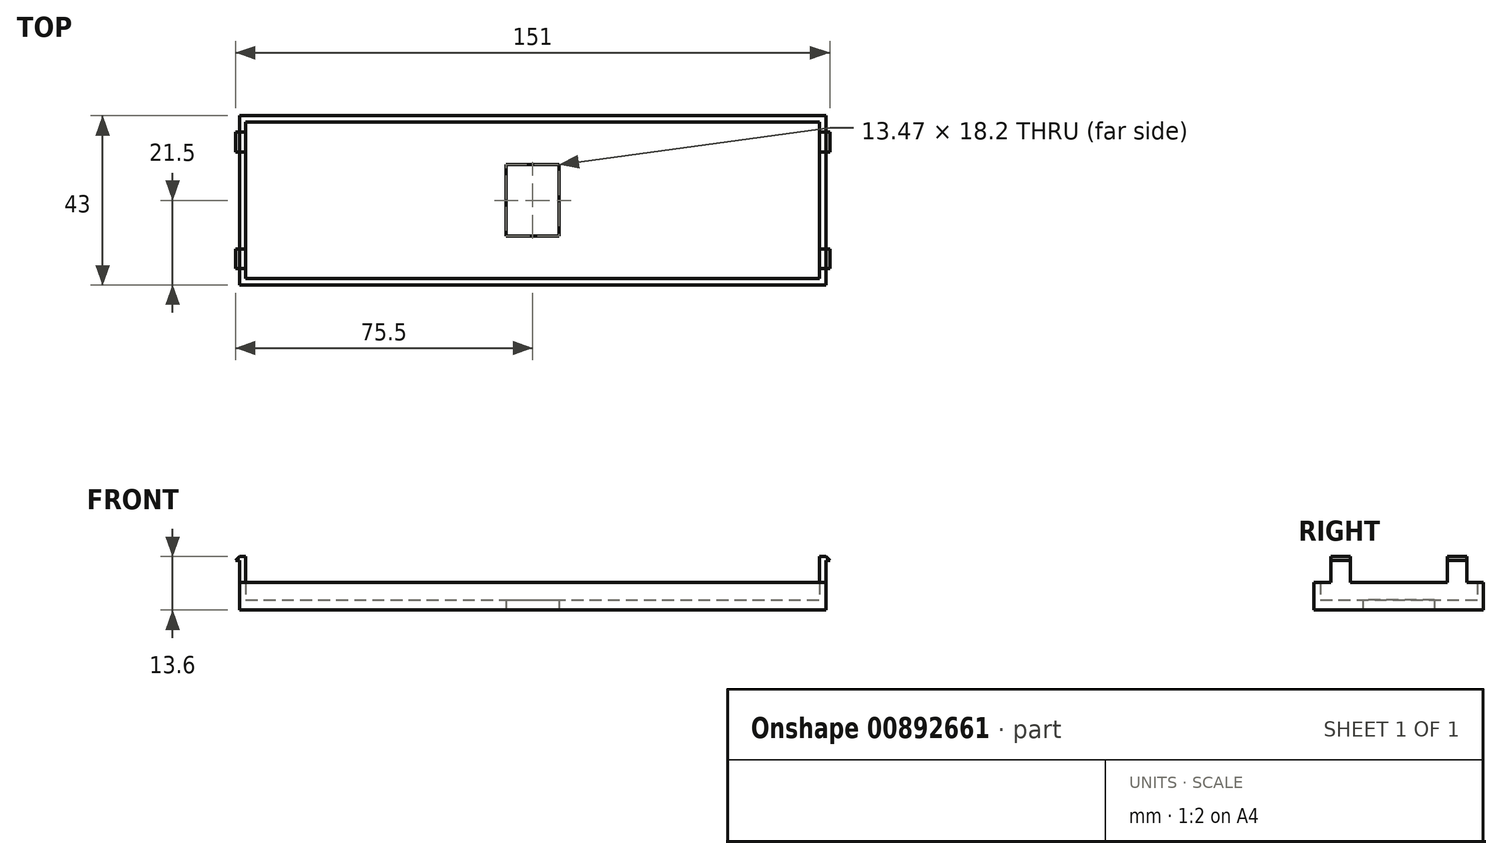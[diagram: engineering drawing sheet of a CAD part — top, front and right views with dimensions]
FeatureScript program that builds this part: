
annotation { "Feature Type Name" : "Feature", "Feature Type Description" : "" }
export const myFeature = defineFeature(function(context is Context, id is Id, definition is map)
    precondition{}
    {
        {
            var Q0;
            Q0=qCreatedBy(makeId("Top.planeOp"),FACE);
            var sketch = newSketch(context, id + "F0", { "sketchPlane" : qUnion([Q0])});
            skLineSegment(sketch, "E0", {"start": v(0, 0) * mm, "end": v(149, 0) * mm});
            skLineSegment(sketch, "E1", {"start": v(149, 0) * mm, "end": v(149, -43) * mm});
            skLineSegment(sketch, "E2", {"start": v(149, -43) * mm, "end": v(0, -43) * mm});
            skLineSegment(sketch, "E3", {"start": v(0, -43) * mm, "end": v(0, 0) * mm});
            skSolve(sketch);
        }
        {
            var Q0;
            Q0 = qSketchRegion(id + "F0", true);
            extrude(context, id + "F1", {"entities" : qUnion([Q0]), "depth" : 7 * mm, "offsetDistance" : 25 * mm});
        }
        {
            var Q0;
            Q0=makeQuery(id+"F1.opExtrude","CAP_FACE",FACE,{"disambiguationData":[OSD([sQuery(id+"F0.wireOp",EDGE,"E0"),sQuery(id+"F0.wireOp",EDGE,"E1"),sQuery(id+"F0.wireOp",EDGE,"E2"),sQuery(id+"F0.wireOp",EDGE,"E3")])],"isStart":false});
            shell(context, id + "F2", {"entities" : qUnion([Q0]), "thickness" : 1.6 * mm});
        }
        {
            var Q0;
            Q0=makeQuery(id+"F2.opShell","OFFSET_FACE",FACE,{"disambiguationData":[OSD([sQuery(id+"F0.wireOp",EDGE,"E0"),sQuery(id+"F0.wireOp",EDGE,"E1"),sQuery(id+"F0.wireOp",EDGE,"E2"),sQuery(id+"F0.wireOp",EDGE,"E3")])]});
            extrude(context, id + "F3", {"entities" : qUnion([Q0]), "operationType" : NewBodyOperationType.ADD, "depth" : 1 * mm, "offsetDistance" : 25 * mm});
        }
        {
            var Q0;
            Q0=makeQuery(id+"F1.opExtrude","CAP_FACE",FACE,{"disambiguationData":[OSD([sQuery(id+"F0.wireOp",EDGE,"E0"),sQuery(id+"F0.wireOp",EDGE,"E1"),sQuery(id+"F0.wireOp",EDGE,"E2"),sQuery(id+"F0.wireOp",EDGE,"E3")])],"isStart":false});
            var sketch = newSketch(context, id + "F4", { "sketchPlane" : qUnion([Q0])});
            skLineSegment(sketch, "E4", {"start": v(1.6, -4.2) * mm, "end": v(0, -4.2) * mm});
            skLineSegment(sketch, "E5", {"start": v(0, -4.2) * mm, "end": v(0, -9.2) * mm});
            skLineSegment(sketch, "E6", {"start": v(0, -9.2) * mm, "end": v(1.6, -9.2) * mm});
            skLineSegment(sketch, "E7", {"start": v(1.6, -9.2) * mm, "end": v(1.6, -4.2) * mm});
            skLineSegment(sketch, "E8", {"start": v(74.5, -1.6) * mm, "end": v(74.5, -47.8) * mm});
            skLineSegment(sketch, "E9.bottom", {"start": v(0, -38.8) * mm, "end": v(1.6, -38.8) * mm});
            skLineSegment(sketch, "E9.top", {"start": v(0, -33.8) * mm, "end": v(1.6, -33.8) * mm});
            skLineSegment(sketch, "E9.left", {"start": v(0, -38.8) * mm, "end": v(0, -33.8) * mm});
            skLineSegment(sketch, "E9.right", {"start": v(1.6, -38.8) * mm, "end": v(1.6, -33.8) * mm});
            skLineSegment(sketch, "E10.MirrorCS", {"start": v(147.4, -9.2) * mm, "end": v(147.4, -4.2) * mm});
            skLineSegment(sketch, "E11.MirrorCS", {"start": v(147.4, -4.2) * mm, "end": v(149, -4.2) * mm});
            skLineSegment(sketch, "E12.MirrorCS", {"start": v(149, -4.2) * mm, "end": v(149, -9.2) * mm});
            skLineSegment(sketch, "E13.MirrorCS", {"start": v(149, -9.2) * mm, "end": v(147.4, -9.2) * mm});
            skLineSegment(sketch, "E14.MirrorCS", {"start": v(149, -33.8) * mm, "end": v(147.4, -33.8) * mm});
            skLineSegment(sketch, "E15.MirrorCS", {"start": v(149, -38.8) * mm, "end": v(149, -33.8) * mm});
            skLineSegment(sketch, "E16.MirrorCS", {"start": v(147.4, -38.8) * mm, "end": v(147.4, -33.8) * mm});
            skLineSegment(sketch, "E17.MirrorCS", {"start": v(149, -38.8) * mm, "end": v(147.4, -38.8) * mm});
            skSolve(sketch);
        }
        {
            var Q0;
            Q0 = qSketchRegion(id + "F4", true);
            extrude(context, id + "F5", {"entities" : qUnion([Q0]), "operationType" : NewBodyOperationType.ADD, "depth" : 6.6 * mm, "offsetDistance" : 25 * mm});
        }
        {
            var Q0;
            Q0=makeQuery(id+"F5.boolean.opBoolean","MERGE",FACE,{"derivedFrom":[makeQuery(id+"F1.opExtrude","SWEPT_FACE",FACE,{"disambiguationData":[OSD([sQuery(id+"F0.wireOp",EDGE,"E3")])]}),makeQuery(id+"F5.opExtrude","SWEPT_FACE",FACE,{"disambiguationData":[OSD([sQuery(id+"F4.wireOp",EDGE,"E5")])]}),makeQuery(id+"F5.opExtrude","SWEPT_FACE",FACE,{"disambiguationData":[OSD([sQuery(id+"F4.wireOp",EDGE,"E9.left")])]})]});
            var sketch = newSketch(context, id + "F6", { "sketchPlane" : qUnion([Q0])});
            skLineSegment(sketch, "E18.bottom", {"start": v(4.2, 13.6) * mm, "end": v(9.2, 13.6) * mm});
            skLineSegment(sketch, "E18.top", {"start": v(4.2, 12.56) * mm, "end": v(9.2, 12.56) * mm});
            skLineSegment(sketch, "E18.left", {"start": v(4.2, 13.6) * mm, "end": v(4.2, 12.56) * mm});
            skLineSegment(sketch, "E18.right", {"start": v(9.2, 13.6) * mm, "end": v(9.2, 12.56) * mm});
            skLineSegment(sketch, "E19.bottom", {"start": v(33.8, 13.6) * mm, "end": v(38.8, 13.6) * mm});
            skLineSegment(sketch, "E19.top", {"start": v(33.8, 12.56) * mm, "end": v(38.8, 12.56) * mm});
            skLineSegment(sketch, "E19.left", {"start": v(33.8, 13.6) * mm, "end": v(33.8, 12.56) * mm});
            skLineSegment(sketch, "E19.right", {"start": v(38.8, 13.6) * mm, "end": v(38.8, 12.56) * mm});
            skSolve(sketch);
        }
        {
            var Q0;
            Q0 = qSketchRegion(id + "F6", true);
            extrude(context, id + "F7", {"entities" : qUnion([Q0]), "operationType" : NewBodyOperationType.ADD, "depth" : 1 * mm, "offsetDistance" : 25 * mm});
        }
        {
            var Q0;
            Q0=makeQuery(id+"F7.opExtrude","CAP_EDGE",EDGE,{"disambiguationData":[OSD([sQuery(id+"F6.wireOp",EDGE,"E18.bottom")])],"isStart":false});
            var Q1;
            Q1=makeQuery(id+"F7.opExtrude","CAP_EDGE",EDGE,{"disambiguationData":[OSD([sQuery(id+"F6.wireOp",EDGE,"E19.bottom")])],"isStart":false});
            chamfer(context, id + "F8", {"entities" : qUnion([Q0, Q1]), "width" : 1 * mm, "tangentPropagation" : true});
        }
        {
            var Q0;
            Q0=makeQuery(id+"F5.boolean.opBoolean","MERGE",FACE,{"derivedFrom":[makeQuery(id+"F1.opExtrude","SWEPT_FACE",FACE,{"disambiguationData":[OSD([sQuery(id+"F0.wireOp",EDGE,"E1")])]}),makeQuery(id+"F5.opExtrude","SWEPT_FACE",FACE,{"disambiguationData":[OSD([sQuery(id+"F4.wireOp",EDGE,"E12.MirrorCS")])]}),makeQuery(id+"F5.opExtrude","SWEPT_FACE",FACE,{"disambiguationData":[OSD([sQuery(id+"F4.wireOp",EDGE,"E15.MirrorCS")])]})]});
            var sketch = newSketch(context, id + "F9", { "sketchPlane" : qUnion([Q0])});
            skLineSegment(sketch, "E20.bottom", {"start": v(-38.8, 13.6) * mm, "end": v(-33.8, 13.6) * mm});
            skLineSegment(sketch, "E20.top", {"start": v(-38.8, 12.59) * mm, "end": v(-33.8, 12.59) * mm});
            skLineSegment(sketch, "E20.left", {"start": v(-38.8, 13.6) * mm, "end": v(-38.8, 12.59) * mm});
            skLineSegment(sketch, "E20.right", {"start": v(-33.8, 13.6) * mm, "end": v(-33.8, 12.59) * mm});
            skLineSegment(sketch, "E21.bottom", {"start": v(-9.2, 13.6) * mm, "end": v(-4.2, 13.6) * mm});
            skLineSegment(sketch, "E21.top", {"start": v(-9.2, 12.59) * mm, "end": v(-4.2, 12.59) * mm});
            skLineSegment(sketch, "E21.left", {"start": v(-9.2, 13.6) * mm, "end": v(-9.2, 12.59) * mm});
            skLineSegment(sketch, "E21.right", {"start": v(-4.2, 13.6) * mm, "end": v(-4.2, 12.59) * mm});
            skSolve(sketch);
        }
        {
            var Q0;
            Q0 = qSketchRegion(id + "F9", true);
            extrude(context, id + "F10", {"entities" : qUnion([Q0]), "operationType" : NewBodyOperationType.ADD, "depth" : 1 * mm, "offsetDistance" : 25 * mm});
        }
        {
            var Q0;
            Q0=makeQuery(id+"F10.opExtrude","CAP_EDGE",EDGE,{"disambiguationData":[OSD([sQuery(id+"F9.wireOp",EDGE,"E20.bottom")])],"isStart":false});
            var Q1;
            Q1=makeQuery(id+"F10.opExtrude","CAP_EDGE",EDGE,{"disambiguationData":[OSD([sQuery(id+"F9.wireOp",EDGE,"E21.bottom")])],"isStart":false});
            chamfer(context, id + "F11", {"entities" : qUnion([Q0, Q1]), "width" : 1 * mm, "tangentPropagation" : true});
        }
        {
            var Q0;
            Q0=makeQuery(id+"F1.opExtrude","CAP_FACE",FACE,{"disambiguationData":[OSD([sQuery(id+"F0.wireOp",EDGE,"E0"),sQuery(id+"F0.wireOp",EDGE,"E1"),sQuery(id+"F0.wireOp",EDGE,"E2"),sQuery(id+"F0.wireOp",EDGE,"E3")])],"isStart":true});
            var sketch = newSketch(context, id + "F12", { "sketchPlane" : qUnion([Q0])});
            skLineSegment(sketch, "E22", {"start": v(74.5, 43) * mm, "end": v(74.5, 0) * mm});
            skLineSegment(sketch, "E23", {"start": v(0, 21.5) * mm, "end": v(149, 21.5) * mm});
            skLineSegment(sketch, "E24.bottom", {"start": v(81.24, 30.6) * mm, "end": v(67.76, 30.6) * mm});
            skLineSegment(sketch, "E24.top", {"start": v(81.24, 12.4) * mm, "end": v(67.76, 12.4) * mm});
            skLineSegment(sketch, "E24.left", {"start": v(81.24, 30.6) * mm, "end": v(81.24, 12.4) * mm});
            skLineSegment(sketch, "E24.right", {"start": v(67.76, 30.6) * mm, "end": v(67.76, 12.4) * mm});
            skPoint(sketch, "E24.middle", {"position": v(74.5, 21.5) * mm});
            skSolve(sketch);
        }
        {
            var Q0;
            Q0 = qSketchRegion(id + "F12", true);
            extrude(context, id + "F13", {"entities" : qUnion([Q0]), "operationType" : NewBodyOperationType.REMOVE, "oppositeDirection" : true, "depth" : 25 * mm, "offsetDistance" : 25 * mm});
        }
    });
